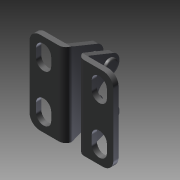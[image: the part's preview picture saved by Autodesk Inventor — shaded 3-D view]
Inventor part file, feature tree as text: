
AUTODESK INVENTOR PART (.ipt)
format: ipt  version: 2011 SP1 (Build 150282100, 282)  size: 224,256 bytes
history: native  units: mm
features: other x14, sketch x10, extrude x8, revolve x2
ambient origin geometry x8: Origin, YZ Plane, XZ Plane, XY Plane, X Axis, Y Axis, Z Axis, Center Point
bodies: Solid1 (feature_tree)
feature tree (34):
  extrude  "Extrusion1"  TaperAngle=360.0deg  [1 undecoded]
  revolve  "Revolution1"  [1 undecoded]
  revolve  "Revolution2"  [1 undecoded]
  extrude  "Extrusion2"  Depth=5.0mm TaperAngle=0.0deg
  extrude  "Extrusion3"  Depth=3.0mm TaperAngle=0.0deg
  extrude  "Extrusion4"  [1 undecoded]
  extrude  "Extrusion5"  [1 undecoded]
  extrude  "Extrusion6"  [1 undecoded]
  extrude  "Extrusion7"  [1 undecoded]
  extrude  "Extrusion8"  [1 undecoded]
  other  "WF1_XY"
  other  "WF1_YZ"
  other  "WF1_ZX"
  other  "WF1_X"
  other  "WF1_Y"
  other  "WF1_Z"
  other  "WF1_Center"
  other  "WF2_XY"
  other  "WF2_YZ"
  other  "WF2_ZX"
  other  "WF2_X"
  other  "WF2_Y"
  other  "WF2_Z"
  other  "WF2_Center"
  sketch  "Skizze_1"  dims[d0=23.876mm d1=0.0mm d2=360.0deg]
  sketch  "Skizze_2"  dims[d3=360.0deg d4=23.876mm d5=0.0mm]
  sketch  "Skizze_3"  dims[d6=50.0mm d7=0.0mm d8=5.0mm d9=0.0mm]
  sketch  "Skizze_4"  dims[d10=1.5mm d11=0.0mm d12=5.0mm d13=0.0mm]
  sketch  "Skizze_5"  dims[d14=5.0mm d15=0.0mm d16=3.0mm d17=0.0mm]
  sketch  "Skizze_6"
  sketch  "Skizze_7"
  sketch  "Skizze_8"
  sketch  "Skizze_10"
  sketch  "Skizze_11"
note: 8 required parameter values undecoded (feature->parameter linkage not recoverable at this tier; creation-order binding heuristic only, values carry confidence <= 0.55)